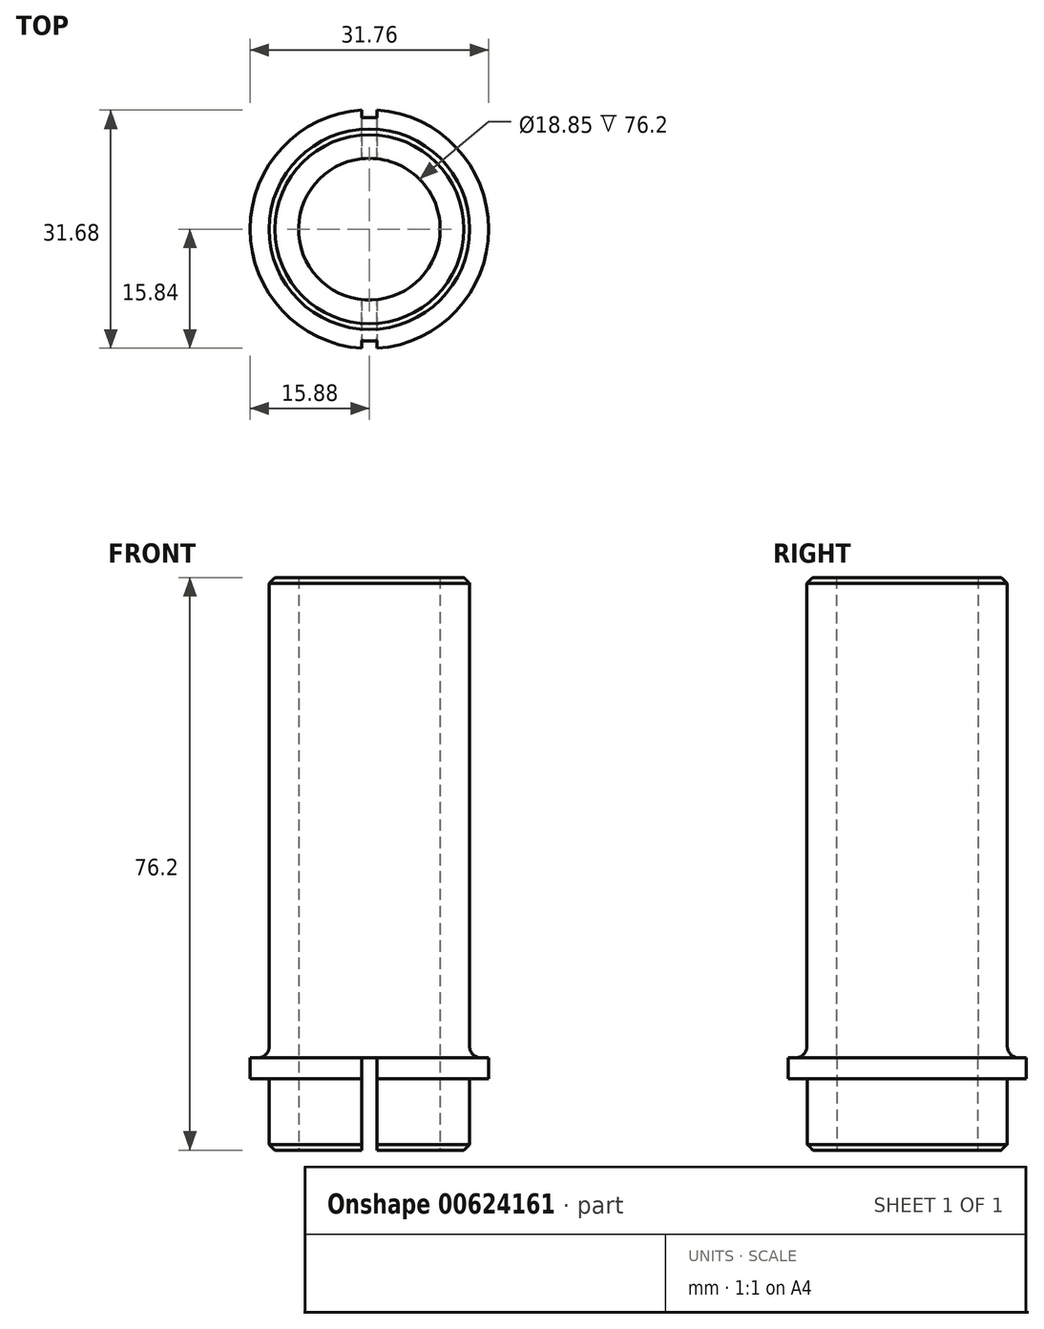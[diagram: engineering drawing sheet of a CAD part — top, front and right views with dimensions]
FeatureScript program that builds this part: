
annotation { "Feature Type Name" : "Feature", "Feature Type Description" : "" }
export const myFeature = defineFeature(function(context is Context, id is Id, definition is map)
    precondition{}
    {
        {
            var Q0;
            Q0=qCreatedBy(makeId("Top.planeOp"),FACE);
            var sketch = newSketch(context, id + "F0", { "sketchPlane" : qUnion([Q0])});
            skCircle(sketch, "E0", {"center": v(0, 0) * mm, "radius": 13.34 * mm});
            skCircle(sketch, "E1.0", {"center": v(0, 0) * mm, "radius": 9.42 * mm});
            skSolve(sketch);
        }
        {
            var Q0;
            Q0 = qSketchRegion(id + "F0", true);
            extrude(context, id + "F1", {"entities" : qUnion([Q0]), "depth" : 76.2 * mm, "offsetDistance" : 25.4 * mm});
        }
        {
            var Q0;
            Q0=makeQuery(id+"F1.opExtrude","CAP_EDGE",EDGE,{"disambiguationData":[OSD([sQuery(id+"F0.wireOp",EDGE,"E0")])],"isStart":false});
            var Q1;
            Q1=makeQuery(id+"F1.opExtrude","CAP_EDGE",EDGE,{"disambiguationData":[OSD([sQuery(id+"F0.wireOp",EDGE,"E0")])],"isStart":true});
            chamfer(context, id + "F2", {"entities" : qUnion([Q0, Q1]), "width" : 0.76 * mm, "tangentPropagation" : true});
        }
        {
            var Q0;
            Q0=makeQuery(id+"F1.opExtrude","CAP_FACE",FACE,{"disambiguationData":[OSD([sQuery(id+"F0.wireOp",EDGE,"E0"),sQuery(id+"F0.wireOp",EDGE,"E1.0")])],"isStart":true});
            var sketch = newSketch(context, id + "F3", { "sketchPlane" : qUnion([Q0])});
            skCircle(sketch, "E2", {"center": v(0, 0) * mm, "radius": 15.88 * mm});
            skCircle(sketch, "E3.0", {"center": v(0, 0) * mm, "radius": 13.34 * mm});
            skSolve(sketch);
        }
        {
            var Q0;
            Q0 = qSketchRegion(id + "F3", true);
            extrude(context, id + "F4", {"entities" : qUnion([Q0]), "oppositeDirection" : true, "depth" : 12.3 * mm, "offsetDistance" : 25.4 * mm, "hasSecondDirection" : true, "secondDirectionOppositeDirection" : true, "secondDirectionDepth" : 9.52 * mm});
        }
        {
            var Q0;
            Q0=makeQuery(id+"F1.opExtrude","CAP_FACE",FACE,{"disambiguationData":[OSD([sQuery(id+"F0.wireOp",EDGE,"E0"),sQuery(id+"F0.wireOp",EDGE,"E1.0")])],"isStart":true});
            var sketch = newSketch(context, id + "F5", { "sketchPlane" : qUnion([Q0])});
            skLineSegment(sketch, "E4.bottom", {"start": v(1.02, 19.05) * mm, "end": v(-1.02, 19.05) * mm});
            skLineSegment(sketch, "E4.top", {"start": v(1.02, -19.05) * mm, "end": v(-1.02, -19.05) * mm});
            skLineSegment(sketch, "E4.left", {"start": v(1.02, 19.05) * mm, "end": v(1.02, -19.05) * mm});
            skLineSegment(sketch, "E4.right", {"start": v(-1.02, 19.05) * mm, "end": v(-1.02, -19.05) * mm});
            skPoint(sketch, "E4.middle", {"position": v(0, 0) * mm});
            skSolve(sketch);
        }
        {
            var Q0;
            Q0 = qSketchRegion(id + "F5", true);
            var Q1;
            Q1=makeQuery(id+"F4.opExtrude","CAP_FACE",FACE,{"disambiguationData":[OSD([sQuery(id+"F3.wireOp",EDGE,"E2"),sQuery(id+"F3.wireOp",EDGE,"E3.0")])],"isStart":false});
            extrude(context, id + "F6", {"entities" : qUnion([Q0]), "operationType" : NewBodyOperationType.REMOVE, "endBound" : BoundingType.UP_TO_SURFACE, "oppositeDirection" : true, "depth" : 25.4 * mm, "endBoundEntityFace" : qUnion([Q1]), "offsetDistance" : 25.4 * mm});
        }
        {
            var Q0;
            Q0=qCreatedBy(makeId("Front.planeOp"),FACE);
            var sketch = newSketch(context, id + "F7", { "sketchPlane" : qUnion([Q0])});
            skLineSegment(sketch, "E5", {"start": v(13.34, 13.82) * mm, "end": v(13.34, 12.3) * mm});
            skLineSegment(sketch, "E6", {"start": v(13.34, 12.3) * mm, "end": v(14.86, 12.3) * mm});
            skArc(sketch, "E7", {"start": v(13.34, 13.82) * mm, "mid": v(13.78, 12.74) * mm, "end": v(14.86, 12.3) * mm});
            skSolve(sketch);
        }
        {
            var Q0;
            Q0 = qSketchRegion(id + "F7", true);
            var Q1;
            Q1=makeQuery(id+"F1.opExtrude","SWEPT_FACE",FACE,{"disambiguationData":[OSD([sQuery(id+"F0.wireOp",EDGE,"E0")])]});
            revolve(context, id + "F8", {"operationType" : NewBodyOperationType.ADD, "entities" : qUnion([Q0]), "axis" : qUnion([Q1]), "revolveType" : RevolveType.FULL});
        }
    });
